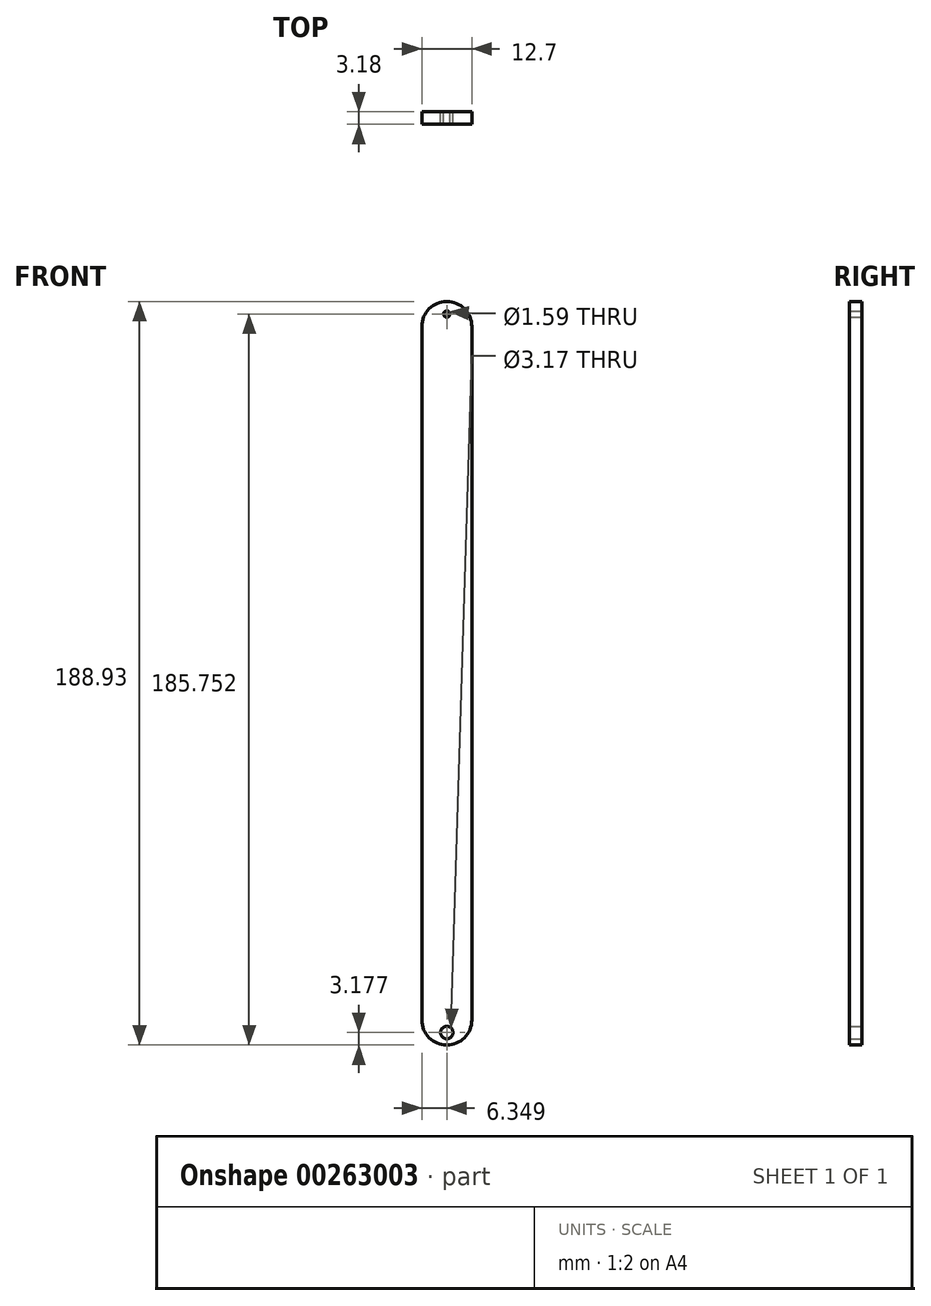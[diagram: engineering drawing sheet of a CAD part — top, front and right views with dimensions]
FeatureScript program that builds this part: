
annotation { "Feature Type Name" : "Feature", "Feature Type Description" : "" }
export const myFeature = defineFeature(function(context is Context, id is Id, definition is map)
    precondition{}
    {
        {
            var Q0;
            Q0=qCreatedBy(makeId("Front.planeOp"),FACE);
            var sketch = newSketch(context, id + "F0", { "sketchPlane" : qUnion([Q0])});
            skLineSegment(sketch, "E0.bottom", {"start": v(1.42, 43.42) * mm, "end": v(1.42, 43.42) * mm});
            skLineSegment(sketch, "E0.top", {"start": v(1.42, -145.5) * mm, "end": v(1.42, -145.5) * mm});
            skLineSegment(sketch, "E0.left", {"start": v(-4.93, 37.07) * mm, "end": v(-4.93, -139.16) * mm});
            skLineSegment(sketch, "E0.right", {"start": v(7.77, 37.07) * mm, "end": v(7.77, -139.16) * mm});
            skPoint(sketch, "E1.visualSharp", {"position": v(-4.93, 43.42) * mm});
            skArc(sketch, "E1.filletArc", {"start": v(1.42, 43.42) * mm, "mid": v(-3.07, 41.56) * mm, "end": v(-4.93, 37.07) * mm});
            skPoint(sketch, "E2.visualSharp", {"position": v(7.77, 43.42) * mm});
            skArc(sketch, "E2.filletArc", {"start": v(7.77, 37.07) * mm, "mid": v(5.9, 41.56) * mm, "end": v(1.42, 43.42) * mm});
            skPoint(sketch, "E3.visualSharp", {"position": v(-4.93, -145.5) * mm});
            skArc(sketch, "E3.filletArc", {"start": v(-4.93, -139.16) * mm, "mid": v(-3.07, -143.65) * mm, "end": v(1.42, -145.5) * mm});
            skPoint(sketch, "E4.visualSharp", {"position": v(7.77, -145.5) * mm});
            skArc(sketch, "E4.filletArc", {"start": v(1.42, -145.5) * mm, "mid": v(5.9, -143.65) * mm, "end": v(7.77, -139.16) * mm});
            skCircle(sketch, "E5", {"center": v(1.42, 40.24) * mm, "radius": 0.8 * mm});
            skCircle(sketch, "E6", {"center": v(1.42, -142.33) * mm, "radius": 1.59 * mm});
            skSolve(sketch);
        }
        {
            var Q0;
            Q0=makeQuery(id+"F0.imprint","IMPRINT",FACE,{"disambiguationData":[TD([[makeQuery(id+"F0.imprint","IMPRINT",EDGE,{"derivedFrom":sQuery(id+"F0.wireOp",EDGE,"E0.left")}),1.0]])]});
            extrude(context, id + "F1", {"entities" : qUnion([Q0]), "depth" : 3.17 * mm});
        }
    });
